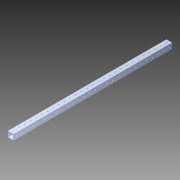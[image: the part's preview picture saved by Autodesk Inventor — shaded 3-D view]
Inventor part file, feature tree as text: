
AUTODESK INVENTOR PART (.ipt)
format: ipt  version: 2014 SP1 (Build 180222100, 222)  size: 1,251,328 bytes
history: native  units: in
note: dims shown in document units (in); Inventor stores cm internally (conversion verified against a paired STEP export)
features: pattern_circular x1, other x1, extrude x1, imported_body x1, sketch x1
ambient origin geometry x8: Origin, YZ Plane, XZ Plane, XY Plane, X Axis, Y Axis, Z Axis, Center Point
bodies: Body1 (feature_tree)
feature tree (5):
  pattern_circular  "CirPattern2"
  other  "1x1 tube1"
  extrude  "Extrusion1"  [1 undecoded]
  imported_body  "Base1"
  sketch  "Sketch1"  dims[d0=31.0in d1=0.0in]
note: 1 required parameter value undecoded (feature->parameter linkage not recoverable at this tier; creation-order binding heuristic only, values carry confidence <= 0.55)
